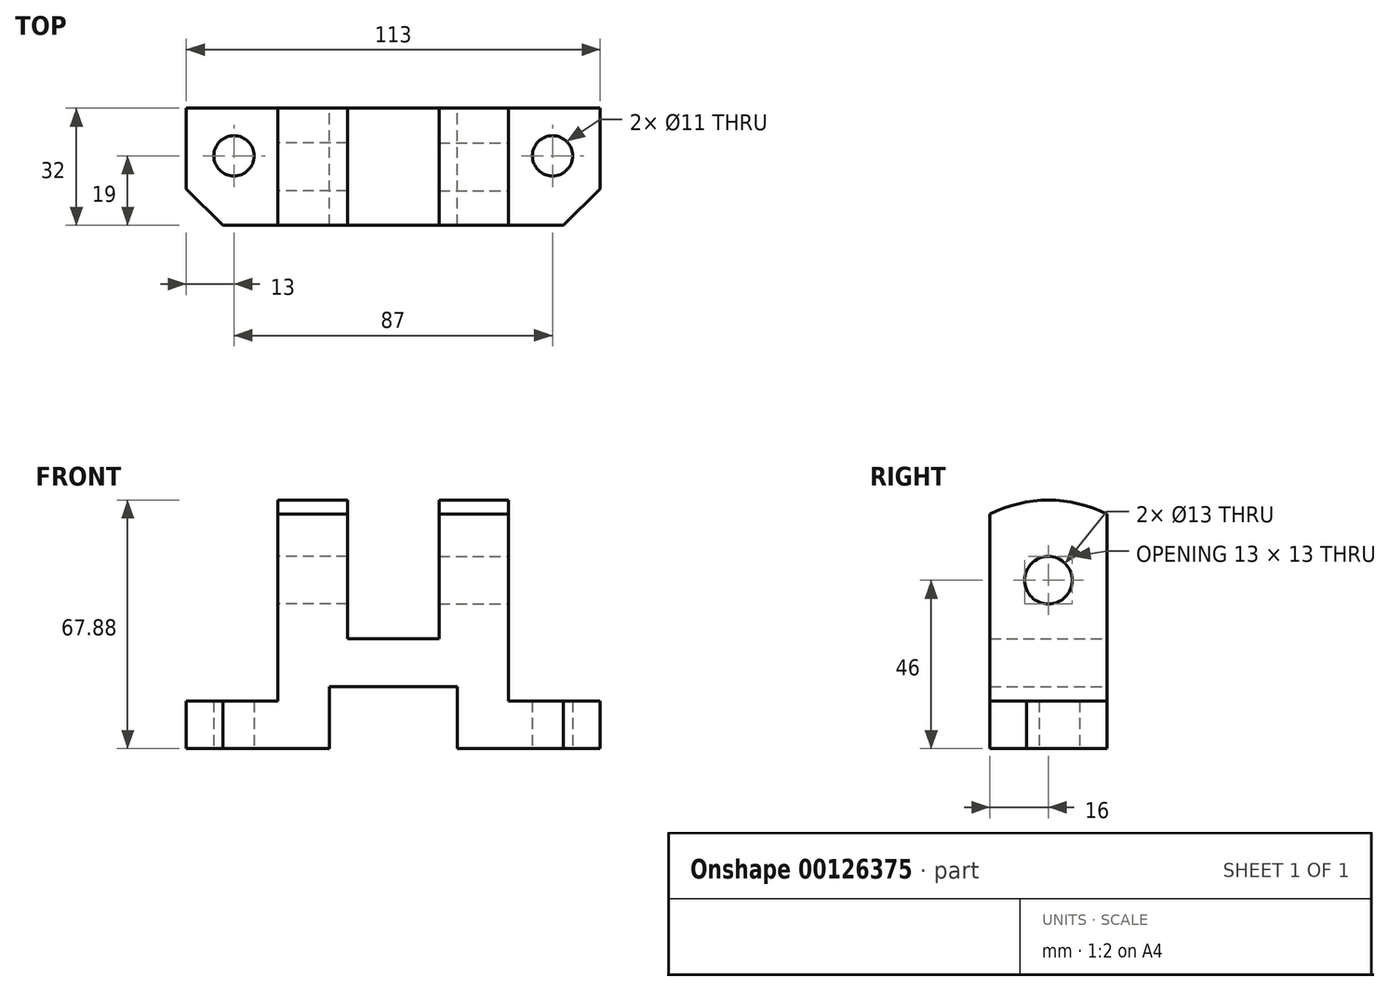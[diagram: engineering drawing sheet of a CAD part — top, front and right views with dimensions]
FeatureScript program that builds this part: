
annotation { "Feature Type Name" : "Feature", "Feature Type Description" : "" }
export const myFeature = defineFeature(function(context is Context, id is Id, definition is map)
    precondition{}
    {
        {
            var Q0;
            Q0=qCreatedBy(makeId("Front.planeOp"),FACE);
            var sketch = newSketch(context, id + "F0", { "sketchPlane" : qUnion([Q0])});
            skLineSegment(sketch, "E0", {"start": v(0, 0) * mm, "end": v(0, 13) * mm});
            skLineSegment(sketch, "E1", {"start": v(0, 13) * mm, "end": v(25, 13) * mm});
            skLineSegment(sketch, "E2", {"start": v(25, 13) * mm, "end": v(25, 64.01) * mm});
            skLineSegment(sketch, "E3", {"start": v(25, 64.01) * mm, "end": v(44, 64.01) * mm});
            skLineSegment(sketch, "E4", {"start": v(44, 64.01) * mm, "end": v(44, 30) * mm});
            skLineSegment(sketch, "E5", {"start": v(44, 30) * mm, "end": v(69, 30) * mm});
            skLineSegment(sketch, "E6", {"start": v(69, 30) * mm, "end": v(69, 64.01) * mm});
            skLineSegment(sketch, "E7", {"start": v(69, 64.01) * mm, "end": v(88, 64.01) * mm});
            skLineSegment(sketch, "E8", {"start": v(88, 64.01) * mm, "end": v(88, 13) * mm});
            skLineSegment(sketch, "E9", {"start": v(88, 13) * mm, "end": v(113, 13) * mm});
            skLineSegment(sketch, "E10", {"start": v(113, 13) * mm, "end": v(113, 0) * mm});
            skLineSegment(sketch, "E11", {"start": v(113, 0) * mm, "end": v(74, 0) * mm});
            skLineSegment(sketch, "E12", {"start": v(74, 0) * mm, "end": v(74, 17) * mm});
            skLineSegment(sketch, "E13", {"start": v(74, 17) * mm, "end": v(39, 17) * mm});
            skLineSegment(sketch, "E14", {"start": v(39, 17) * mm, "end": v(39, 0) * mm});
            skLineSegment(sketch, "E15", {"start": v(0, 0) * mm, "end": v(39, 0) * mm});
            skSolve(sketch);
        }
        {
            var Q0;
            Q0 = qSketchRegion(id + "F0", true);
            extrude(context, id + "F1", {"entities" : qUnion([Q0]), "depth" : 32 * mm});
        }
        {
            var Q0;
            Q0=makeQuery(id+"F1.opExtrude","SWEPT_FACE",FACE,{"disambiguationData":[OSD([sQuery(id+"F0.wireOp",EDGE,"E8")])]});
            var sketch = newSketch(context, id + "F2", { "sketchPlane" : qUnion([Q0])});
            skCircle(sketch, "E16", {"center": v(-16, 46) * mm, "radius": 6.5 * mm});
            skSolve(sketch);
        }
        {
            var Q0;
            Q0=makeQuery(id+"F2.imprint","IMPRINT",FACE,{"disambiguationData":[TD([[makeQuery(id+"F2.imprint","IMPRINT",EDGE,{"derivedFrom":sQuery(id+"F2.wireOp",EDGE,"E16")}),1.0]])]});
            var Q1;
            Q1=sQuery(id+"F2.wireOp",EDGE,"E16");
            extrude(context, id + "F3", {"entities" : qUnion([Q0]), "operationType" : NewBodyOperationType.REMOVE, "surfaceEntities" : qUnion([Q1]), "endBound" : BoundingType.UP_TO_NEXT, "oppositeDirection" : true, "depth" : 25 * mm});
        }
        {
            var Q0;
            Q0=makeQuery(id+"F1.opExtrude","SWEPT_FACE",FACE,{"disambiguationData":[OSD([sQuery(id+"F0.wireOp",EDGE,"E2")])]});
            var sketch = newSketch(context, id + "F4", { "sketchPlane" : qUnion([Q0])});
            skCircle(sketch, "E17", {"center": v(16, 46) * mm, "radius": 6.5 * mm});
            skSolve(sketch);
        }
        {
            var Q0;
            Q0 = qSketchRegion(id + "F4", true);
            extrude(context, id + "F5", {"entities" : qUnion([Q0]), "operationType" : NewBodyOperationType.REMOVE, "endBound" : BoundingType.UP_TO_NEXT, "oppositeDirection" : true, "depth" : 25 * mm});
        }
        {
            var Q0;
            Q0=qCreatedBy(makeId("Top.planeOp"),FACE);
            var sketch = newSketch(context, id + "F6", { "sketchPlane" : qUnion([Q0])});
            skLineSegment(sketch, "E18", {"start": v(0, -32) * mm, "end": v(0, -22) * mm});
            skLineSegment(sketch, "E19", {"start": v(0, -22) * mm, "end": v(10, -32) * mm});
            skLineSegment(sketch, "E20", {"start": v(10, -32) * mm, "end": v(0, -32) * mm});
            skLineSegment(sketch, "E21", {"start": v(103, -32) * mm, "end": v(113, -32) * mm});
            skLineSegment(sketch, "E22", {"start": v(113, -32) * mm, "end": v(113, -22) * mm});
            skLineSegment(sketch, "E23", {"start": v(113, -22) * mm, "end": v(103, -32) * mm});
            skSolve(sketch);
        }
        {
            var Q0;
            Q0 = qSketchRegion(id + "F6", true);
            extrude(context, id + "F7", {"entities" : qUnion([Q0]), "operationType" : NewBodyOperationType.REMOVE, "endBound" : BoundingType.UP_TO_NEXT, "depth" : 25 * mm});
        }
        {
            var Q0;
            Q0=qCreatedBy(makeId("Top.planeOp"),FACE);
            var sketch = newSketch(context, id + "F8", { "sketchPlane" : qUnion([Q0])});
            skCircle(sketch, "E24", {"center": v(13, -13) * mm, "radius": 5.5 * mm});
            skCircle(sketch, "E25", {"center": v(100, -13) * mm, "radius": 5.5 * mm});
            skSolve(sketch);
        }
        {
            var Q0;
            Q0 = qSketchRegion(id + "F8", true);
            extrude(context, id + "F9", {"entities" : qUnion([Q0]), "operationType" : NewBodyOperationType.REMOVE, "endBound" : BoundingType.UP_TO_NEXT, "depth" : 25 * mm});
        }
        {
            var Q0;
            Q0=makeQuery(id+"F1.opExtrude","SWEPT_FACE",FACE,{"disambiguationData":[OSD([sQuery(id+"F0.wireOp",EDGE,"E8")])]});
            var sketch = newSketch(context, id + "F10", { "sketchPlane" : qUnion([Q0])});
            skArc(sketch, "E26", {"start": v(0, 64.01) * mm, "mid": v(-16, 67.88) * mm, "end": v(-32, 64.01) * mm});
            skLineSegment(sketch, "E27", {"start": v(-32, 64.01) * mm, "end": v(0, 64.01) * mm});
            skSolve(sketch);
        }
        {
            var Q0;
            Q0=makeQuery(id+"F10.imprint","IMPRINT",FACE,{"disambiguationData":[TD([[makeQuery(id+"F10.imprint","IMPRINT",EDGE,{"derivedFrom":sQuery(id+"F10.wireOp",EDGE,"E26")}),1.0]])]});
            var Q1;
            Q1=makeQuery(id+"F1.opExtrude","SWEPT_FACE",FACE,{"disambiguationData":[OSD([sQuery(id+"F0.wireOp",EDGE,"E6")])]});
            extrude(context, id + "F11", {"entities" : qUnion([Q0]), "operationType" : NewBodyOperationType.ADD, "oppositeDirection" : true, "endBoundEntityFace" : qUnion([Q1]), "depth" : 19 * mm});
        }
        {
            var Q0;
            Q0=makeQuery(id+"F4.imprint","IMPRINT",FACE,{"disambiguationData":[TD([[makeQuery(id+"F4.imprint","IMPRINT",EDGE,{"derivedFrom":sQuery(id+"F4.wireOp",EDGE,"E17")}),-1.0]])]});
            var sketch = newSketch(context, id + "F12", { "sketchPlane" : qUnion([Q0])});
            skArc(sketch, "E28", {"start": v(32, 64.01) * mm, "mid": v(16, 67.88) * mm, "end": v(0, 64.01) * mm});
            skLineSegment(sketch, "E29", {"start": v(0, 64.01) * mm, "end": v(32, 64.01) * mm});
            skSolve(sketch);
        }
        {
            var Q0;
            Q0=makeQuery(id+"F12.imprint","IMPRINT",FACE,{"disambiguationData":[TD([[makeQuery(id+"F12.imprint","IMPRINT",EDGE,{"derivedFrom":sQuery(id+"F12.wireOp",EDGE,"E28")}),1.0]])]});
            extrude(context, id + "F13", {"entities" : qUnion([Q0]), "operationType" : NewBodyOperationType.ADD, "oppositeDirection" : true, "depth" : 19 * mm});
        }
    });
